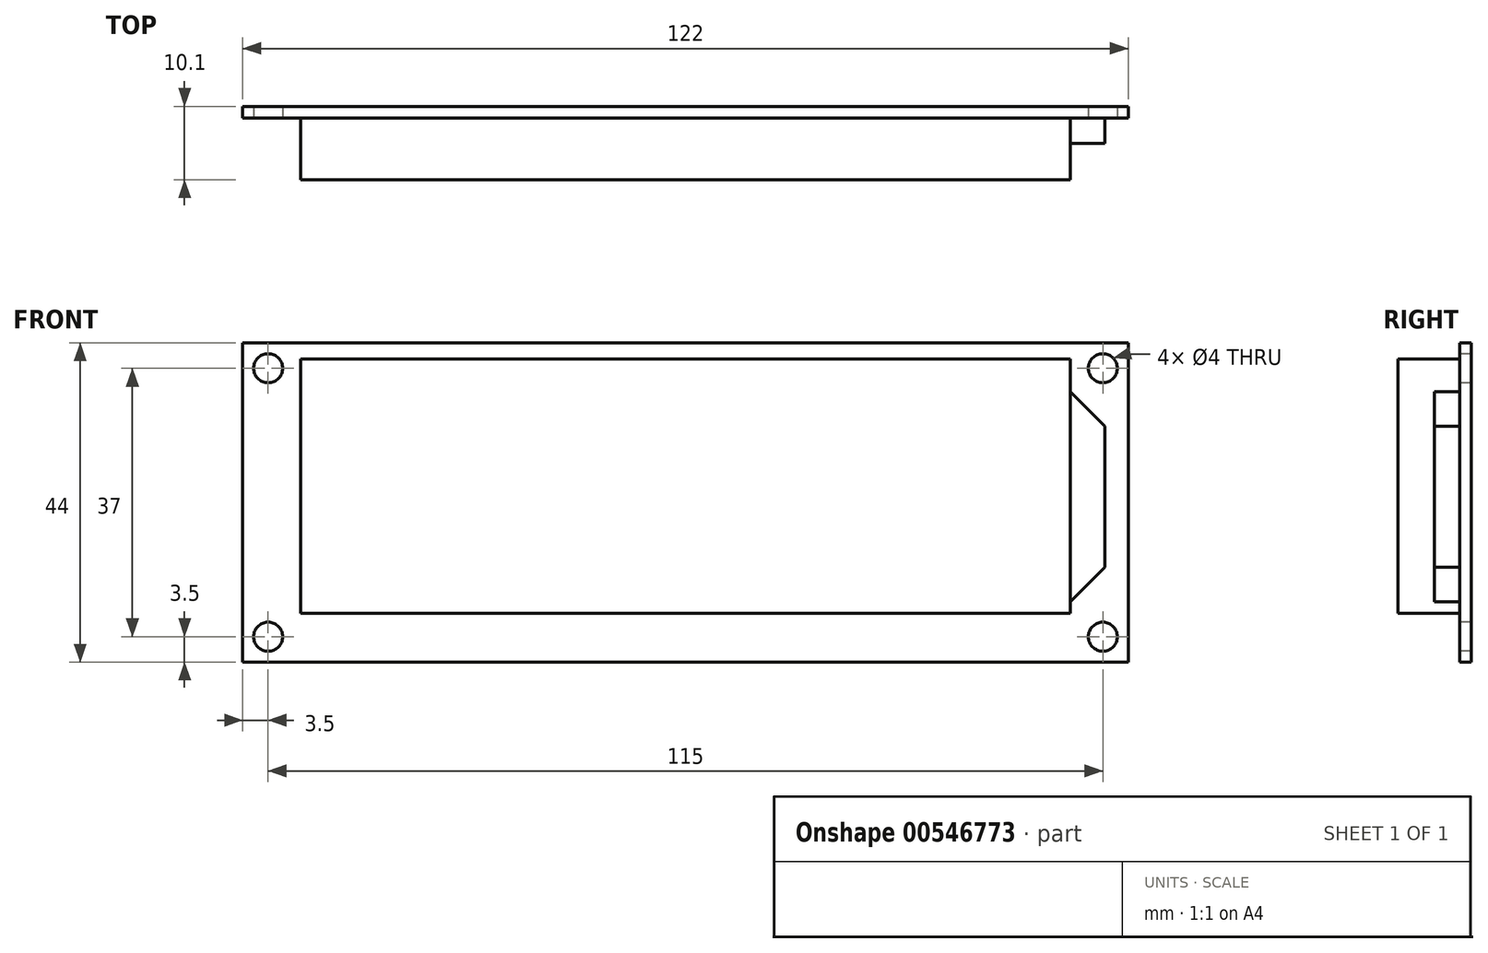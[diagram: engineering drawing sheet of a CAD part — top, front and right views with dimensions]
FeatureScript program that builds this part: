
annotation { "Feature Type Name" : "Feature", "Feature Type Description" : "" }
export const myFeature = defineFeature(function(context is Context, id is Id, definition is map)
    precondition{}
    {
        {
            var Q0;
            Q0=qCreatedBy(makeId("Front.planeOp"),FACE);
            var sketch = newSketch(context, id + "F0", { "sketchPlane" : qUnion([Q0])});
            skLineSegment(sketch, "E0.bottom", {"start": v(-61, 22) * mm, "end": v(61, 22) * mm});
            skLineSegment(sketch, "E0.top", {"start": v(-61, -22) * mm, "end": v(61, -22) * mm});
            skLineSegment(sketch, "E0.left", {"start": v(-61, 22) * mm, "end": v(-61, -22) * mm});
            skLineSegment(sketch, "E0.right", {"start": v(61, 22) * mm, "end": v(61, -22) * mm});
            skPoint(sketch, "E0.middle", {"position": v(0, 0) * mm});
            skPoint(sketch, "E1", {"position": v(-57.5, -18.5) * mm});
            skCircle(sketch, "E2", {"center": v(-57.5, -18.5) * mm, "radius": 2 * mm});
            skCircle(sketch, "E3.MirrorC", {"center": v(-57.5, 18.5) * mm, "radius": 2 * mm});
            skCircle(sketch, "E4.MirrorC", {"center": v(57.5, -18.5) * mm, "radius": 2 * mm});
            skCircle(sketch, "E5.MirrorC", {"center": v(57.5, 18.5) * mm, "radius": 2 * mm});
            skSolve(sketch);
        }
        {
            var Q0;
            Q0=makeQuery(id+"F0.imprint","IMPRINT",FACE,{"disambiguationData":[TD([[makeQuery(id+"F0.imprint","IMPRINT",EDGE,{"derivedFrom":sQuery(id+"F0.wireOp",EDGE,"E0.bottom")}),-1.0]])]});
            extrude(context, id + "F1", {"entities" : qUnion([Q0]), "oppositeDirection" : true, "depth" : 1.6 * mm, "offsetDistance" : 25 * mm});
        }
        {
            var Q0;
            Q0=qCreatedBy(makeId("Front.planeOp"),FACE);
            var sketch = newSketch(context, id + "F2", { "sketchPlane" : qUnion([Q0])});
            skLineSegment(sketch, "E6.bottom", {"start": v(-53, 19.75) * mm, "end": v(53, 19.75) * mm});
            skLineSegment(sketch, "E6.top", {"start": v(-53, -15.25) * mm, "end": v(53, -15.25) * mm});
            skLineSegment(sketch, "E6.left", {"start": v(-53, 19.75) * mm, "end": v(-53, -15.25) * mm});
            skLineSegment(sketch, "E6.right", {"start": v(53, 19.75) * mm, "end": v(53, -15.25) * mm});
            skSolve(sketch);
        }
        {
            var Q0;
            Q0 = qSketchRegion(id + "F2", true);
            var Q1;
            Q1=makeQuery(id+"F1.opExtrude","CAP_FACE",FACE,{"disambiguationData":[OSD([sQuery(id+"F0.wireOp",EDGE,"E0.bottom"),sQuery(id+"F0.wireOp",EDGE,"E0.top"),sQuery(id+"F0.wireOp",EDGE,"E0.left"),sQuery(id+"F0.wireOp",EDGE,"E0.right"),sQuery(id+"F0.wireOp",EDGE,"E2"),sQuery(id+"F0.wireOp",EDGE,"E3.MirrorC"),sQuery(id+"F0.wireOp",EDGE,"E4.MirrorC"),sQuery(id+"F0.wireOp",EDGE,"E5.MirrorC")])],"isStart":true});
            var Q2;
            Q2=makeQuery(id+"F1.opExtrude","SWEPT_BODY",BODY,{"disambiguationData":[OSD([sQuery(id+"F0.wireOp",EDGE,"E0.bottom"),sQuery(id+"F0.wireOp",EDGE,"E0.top"),sQuery(id+"F0.wireOp",EDGE,"E0.left"),sQuery(id+"F0.wireOp",EDGE,"E0.right"),sQuery(id+"F0.wireOp",EDGE,"E2"),sQuery(id+"F0.wireOp",EDGE,"E3.MirrorC"),sQuery(id+"F0.wireOp",EDGE,"E4.MirrorC"),sQuery(id+"F0.wireOp",EDGE,"E5.MirrorC")])]});
            extrude(context, id + "F3", {"entities" : qUnion([Q0]), "operationType" : NewBodyOperationType.ADD, "depth" : 8.5 * mm, "endBoundEntityFace" : qUnion([Q1]), "endBoundEntityBody" : qUnion([Q2]), "offsetDistance" : 8.5 * mm});
        }
        {
            var Q0;
            Q0=qCreatedBy(makeId("Front.planeOp"),FACE);
            var sketch = newSketch(context, id + "F4", { "sketchPlane" : qUnion([Q0])});
            skLineSegment(sketch, "E7", {"start": v(53, -13.7) * mm, "end": v(53, 15.3) * mm});
            skLineSegment(sketch, "E8", {"start": v(53, 15.3) * mm, "end": v(57.8, 10.5) * mm});
            skLineSegment(sketch, "E9", {"start": v(57.8, 10.5) * mm, "end": v(57.8, -8.9) * mm});
            skLineSegment(sketch, "E10", {"start": v(57.8, -8.9) * mm, "end": v(53, -13.7) * mm});
            skSolve(sketch);
        }
        {
            var Q0;
            Q0 = qSketchRegion(id + "F4", true);
            extrude(context, id + "F5", {"entities" : qUnion([Q0]), "operationType" : NewBodyOperationType.ADD, "depth" : 3.5 * mm, "offsetDistance" : 25 * mm});
        }
    });
